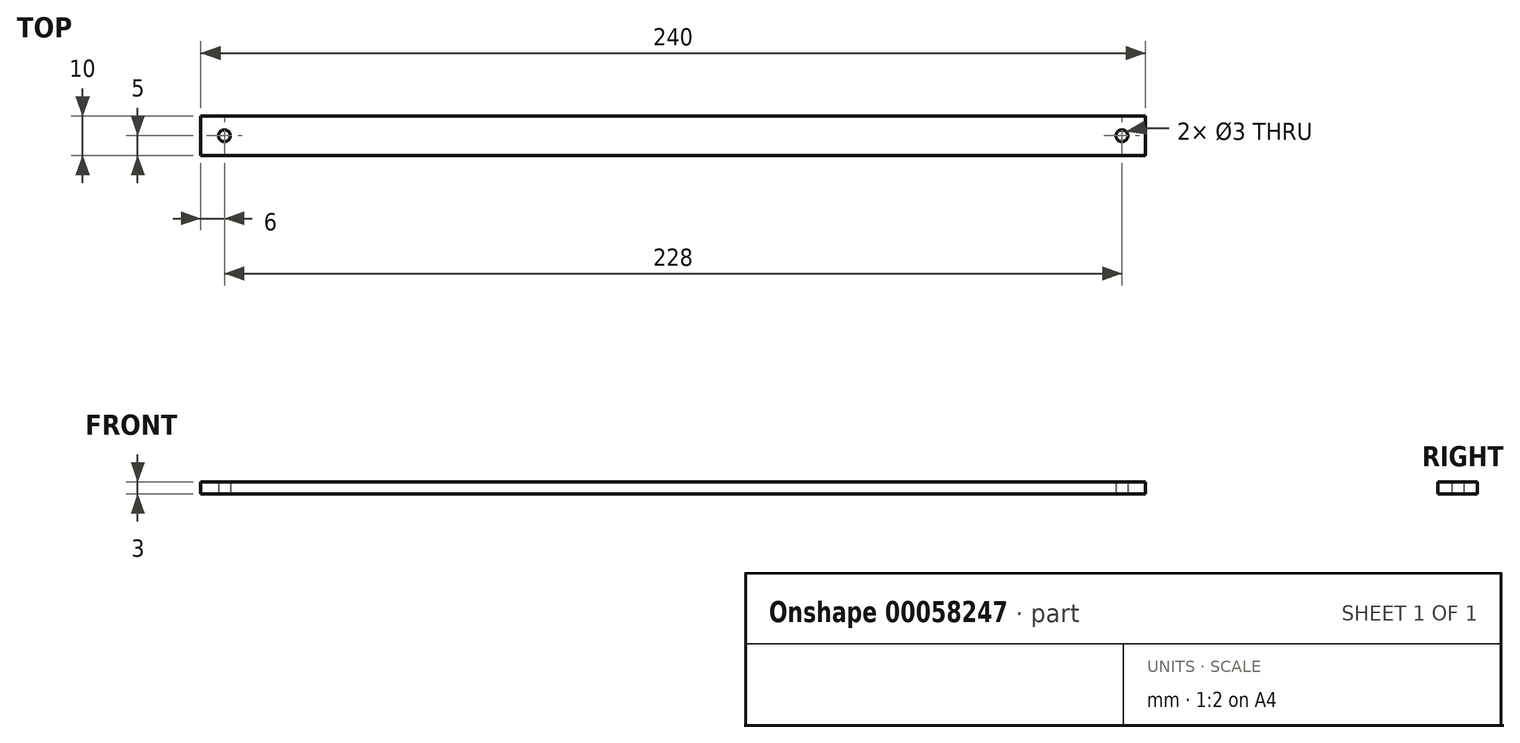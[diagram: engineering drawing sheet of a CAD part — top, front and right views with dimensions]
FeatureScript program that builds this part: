
annotation { "Feature Type Name" : "Feature", "Feature Type Description" : "" }
export const myFeature = defineFeature(function(context is Context, id is Id, definition is map)
    precondition{}
    {
        {
            var Q0;
            Q0=qCreatedBy(makeId("Top.planeOp"),FACE);
            var sketch = newSketch(context, id + "F0", { "sketchPlane" : qUnion([Q0])});
            skLineSegment(sketch, "E0.bottom", {"start": v(120, 5) * mm, "end": v(-120, 5) * mm});
            skLineSegment(sketch, "E0.top", {"start": v(120, -5) * mm, "end": v(-120, -5) * mm});
            skLineSegment(sketch, "E0.left", {"start": v(120, 5) * mm, "end": v(120, -5) * mm});
            skLineSegment(sketch, "E0.right", {"start": v(-120, 5) * mm, "end": v(-120, -5) * mm});
            skPoint(sketch, "E0.middle", {"position": v(0, 0) * mm});
            skLineSegment(sketch, "E1", {"start": v(-120, 0) * mm, "end": v(0, 0) * mm, "construction": true});
            skLineSegment(sketch, "E2", {"start": v(0, 5) * mm, "end": v(0, 0) * mm, "construction": true});
            skCircle(sketch, "E3", {"center": v(-114, 0) * mm, "radius": 1.5 * mm});
            skCircle(sketch, "E4.MirrorC", {"center": v(114, 0) * mm, "radius": 1.5 * mm});
            skSolve(sketch);
        }
        {
            var Q0;
            Q0 = qSketchRegion(id + "F0", true);
            extrude(context, id + "F1", {"entities" : qUnion([Q0]), "depth" : 3 * mm});
        }
    });
